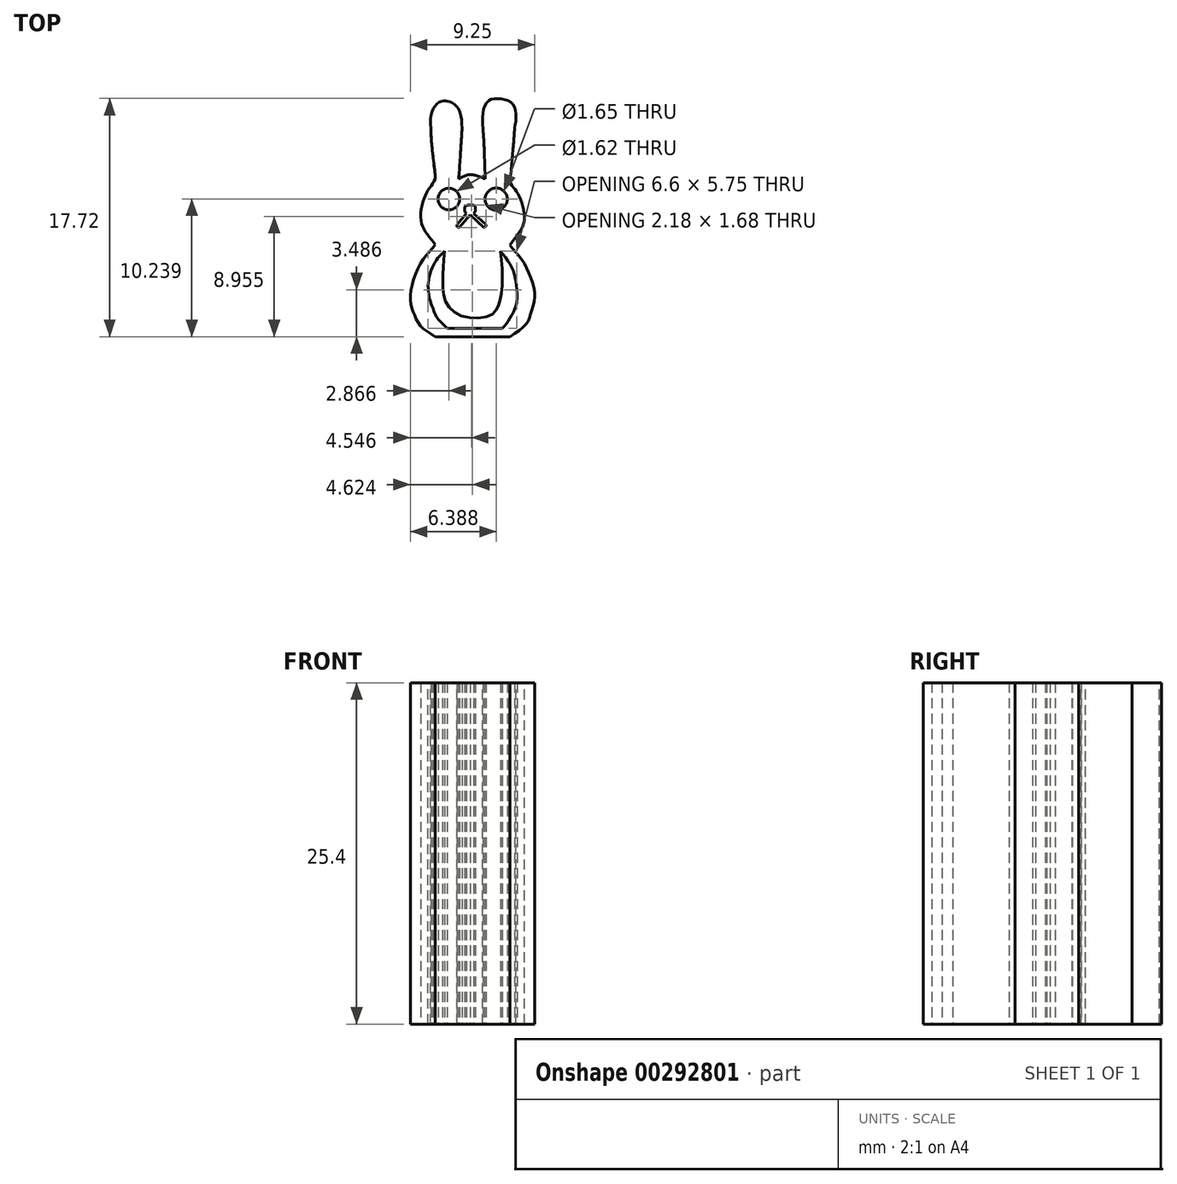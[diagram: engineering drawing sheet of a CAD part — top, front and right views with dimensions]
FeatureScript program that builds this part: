
annotation { "Feature Type Name" : "Feature", "Feature Type Description" : "" }
export const myFeature = defineFeature(function(context is Context, id is Id, definition is map)
    precondition{}
    {
        {
            var Q0;
            Q0=qCreatedBy(makeId("Top.planeOp"),FACE);
            var sketch = newSketch(context, id + "F0", { "sketchPlane" : qUnion([Q0])});
            skFitSpline(sketch, "E0", {"points": [v(-48.95, 35.1) * mm, v(-49.04, 33.63) * mm, v(-49.2, 31.33) * mm], "startDerivative": vector(-0.17, -2.98) * mm, "endDerivative": vector(-0.34, -3.33) * mm});
            skFitSpline(sketch, "E1", {"points": [v(-47.39, 35.1) * mm, v(-47.3, 33.6) * mm, v(-47.22, 31.33) * mm], "startDerivative": vector(0.18, -3.04) * mm, "endDerivative": vector(0.15, -3.27) * mm});
            skFitSpline(sketch, "E2", {"points": [v(-51.26, 35.12) * mm, v(-51.18, 33.71) * mm, v(-50.94, 31.33) * mm, v(-50.94, 31.33) * mm], "startDerivative": vector(0.05, -2.48) * mm, "endDerivative": vector(0.03, 0.02) * mm});
            skFitSpline(sketch, "E3", {"points": [v(-45.03, 35.1) * mm, v(-45.15, 33.55) * mm, v(-45.4, 31.12) * mm], "startDerivative": vector(-0.22, -3.29) * mm, "endDerivative": vector(-0.57, -4.6) * mm});
            skFitSpline(sketch, "E4", {"points": [v(-49.2, 31.33) * mm, v(-48.35, 31.65) * mm, v(-47.22, 31.33) * mm], "startDerivative": vector(1.75, 0.99) * mm, "endDerivative": vector(2.2, -0.95) * mm});
            skFitSpline(sketch, "E5", {"points": [v(-50.94, 31.33) * mm, v(-51.65, 30.16) * mm, v(-51.93, 27.93) * mm, v(-50.94, 26.43) * mm], "startDerivative": vector(-1.76, -4.17) * mm, "endDerivative": vector(3.05, -4.9) * mm});
            skFitSpline(sketch, "E6", {"points": [v(-45.4, 31.12) * mm, v(-44.78, 30.2) * mm, v(-44.35, 28.05) * mm, v(-45.4, 26.4) * mm], "startDerivative": vector(1.7, -3.87) * mm, "endDerivative": vector(-3.58, -5.67) * mm});
            skFitSpline(sketch, "E7", {"points": [v(-50.94, 26.43) * mm, v(-51.79, 25.4) * mm, v(-52.62, 23.6) * mm, v(-52.76, 22.12) * mm, v(-52.5, 21.25) * mm, v(-52.01, 20.37) * mm, v(-50.94, 19.6) * mm], "startDerivative": vector(-4.6, -6.8) * mm, "endDerivative": vector(7.37, -4.66) * mm});
            skFitSpline(sketch, "E8", {"points": [v(-45.4, 26.4) * mm, v(-44.55, 25.4) * mm, v(-43.82, 23.92) * mm, v(-43.55, 22.52) * mm, v(-43.84, 21.3) * mm, v(-44.14, 20.59) * mm, v(-45.4, 19.6) * mm], "startDerivative": vector(4, -6.46) * mm, "endDerivative": vector(-8.46, -5.02) * mm});
            skCircle(sketch, "E9", {"center": v(-46.4, 29.83) * mm, "radius": 0.82 * mm});
            skCircle(sketch, "E10", {"center": v(-49.92, 29.83) * mm, "radius": 0.8 * mm});
            skFitSpline(sketch, "E11", {"points": [v(-48.64, 28.77) * mm, v(-48.75, 28.96) * mm, v(-48.71, 29.28) * mm, v(-48.5, 29.37) * mm, v(-48.23, 29.38) * mm, v(-47.99, 29.29) * mm, v(-47.97, 28.95) * mm, v(-48.07, 28.76) * mm], "startDerivative": vector(-1.03, 1.22) * mm, "endDerivative": vector(-0.9, -1.22) * mm});
            skLineSegment(sketch, "E12", {"start": v(-48.64, 28.77) * mm, "end": v(-49.32, 27.94) * mm});
            skLineSegment(sketch, "E13", {"start": v(-48.07, 28.76) * mm, "end": v(-47.16, 27.94) * mm});
            skFitSpline(sketch, "E14", {"points": [v(-49.32, 27.94) * mm, v(-49.32, 27.78) * mm, v(-49.15, 27.7) * mm], "startDerivative": vector(-0.08, -0.4) * mm, "endDerivative": vector(0.4, -0.08) * mm});
            skFitSpline(sketch, "E15", {"points": [v(-47.16, 27.94) * mm, v(-47.16, 27.84) * mm, v(-47.3, 27.7) * mm], "startDerivative": vector(0.05, -0.28) * mm, "endDerivative": vector(-0.53, -0.34) * mm});
            skLineSegment(sketch, "E16", {"start": v(-48.35, 28.67) * mm, "end": v(-49.15, 27.7) * mm});
            skLineSegment(sketch, "E17", {"start": v(-48.35, 28.67) * mm, "end": v(-47.3, 27.7) * mm});
            skFitSpline(sketch, "E18", {"points": [v(-50.23, 25.95) * mm, v(-50.37, 23.92) * mm, v(-50.23, 22.4) * mm, v(-49.1, 21.17) * mm, v(-46.87, 21.17) * mm, v(-46.27, 21.87) * mm, v(-45.96, 23.4) * mm, v(-46.08, 25.95) * mm], "startDerivative": vector(-2.09, -15.14) * mm, "endDerivative": vector(-1.5, 14.6) * mm});
            skLineSegment(sketch, "E19", {"start": v(-50.94, 19.6) * mm, "end": v(-45.4, 19.6) * mm});
            skLineSegment(sketch, "E20", {"start": v(-47.3, 27.7) * mm, "end": v(-47.3, 27.7) * mm});
            skFitSpline(sketch, "E21", {"points": [v(-51.26, 35.12) * mm, v(-51.26, 36.04) * mm, v(-50.76, 36.95) * mm, v(-50.24, 37.13) * mm, v(-49.84, 37.07) * mm, v(-49.22, 36.55) * mm, v(-48.95, 35.1) * mm], "startDerivative": vector(-0.6, 5.07) * mm, "endDerivative": vector(0.36, -7.4) * mm});
            skFitSpline(sketch, "E22", {"points": [v(-47.39, 35.1) * mm, v(-47.39, 36.27) * mm, v(-46.93, 37.18) * mm, v(-46.2, 37.3) * mm, v(-45.28, 37.01) * mm, v(-44.94, 36.16) * mm, v(-45.03, 35.1) * mm], "startDerivative": vector(-0.58, 6.41) * mm, "endDerivative": vector(-1.02, -6.1) * mm});
            skFitSpline(sketch, "E23", {"points": [v(-46.08, 25.95) * mm, v(-45.25, 24.78) * mm, v(-44.92, 23.55) * mm, v(-44.92, 21.95) * mm, v(-45.38, 20.97) * mm, v(-45.94, 20.2) * mm], "startDerivative": vector(4.28, -5.55) * mm, "endDerivative": vector(-3.88, -3.09) * mm});
            skFitSpline(sketch, "E24", {"points": [v(-50.23, 25.95) * mm, v(-50.9, 25.22) * mm, v(-51.43, 23.83) * mm, v(-51.38, 22.54) * mm, v(-51.13, 21.76) * mm], "startDerivative": vector(-2.99, -2.74) * mm, "endDerivative": vector(1.3, -3.41) * mm});
            skFitSpline(sketch, "E25", {"points": [v(-51.13, 21.76) * mm, v(-50.77, 20.97) * mm, v(-50.06, 20.2) * mm], "startDerivative": vector(0.64, -1.58) * mm, "endDerivative": vector(0.89, -1.2) * mm});
            skLineSegment(sketch, "E26", {"start": v(-50.06, 20.2) * mm, "end": v(-45.94, 20.2) * mm});
            skSolve(sketch);
        }
        {
            var Q0;
            Q0=makeQuery(id+"F0.imprint","IMPRINT",FACE,{"disambiguationData":[TD([[makeQuery(id+"F0.imprint","IMPRINT",EDGE,{"derivedFrom":sQuery(id+"F0.wireOp",EDGE,"E0")}),-1.0]])]});
            extrude(context, id + "F1", {"entities" : qUnion([Q0]), "depth" : 25.4 * mm});
        }
    });
